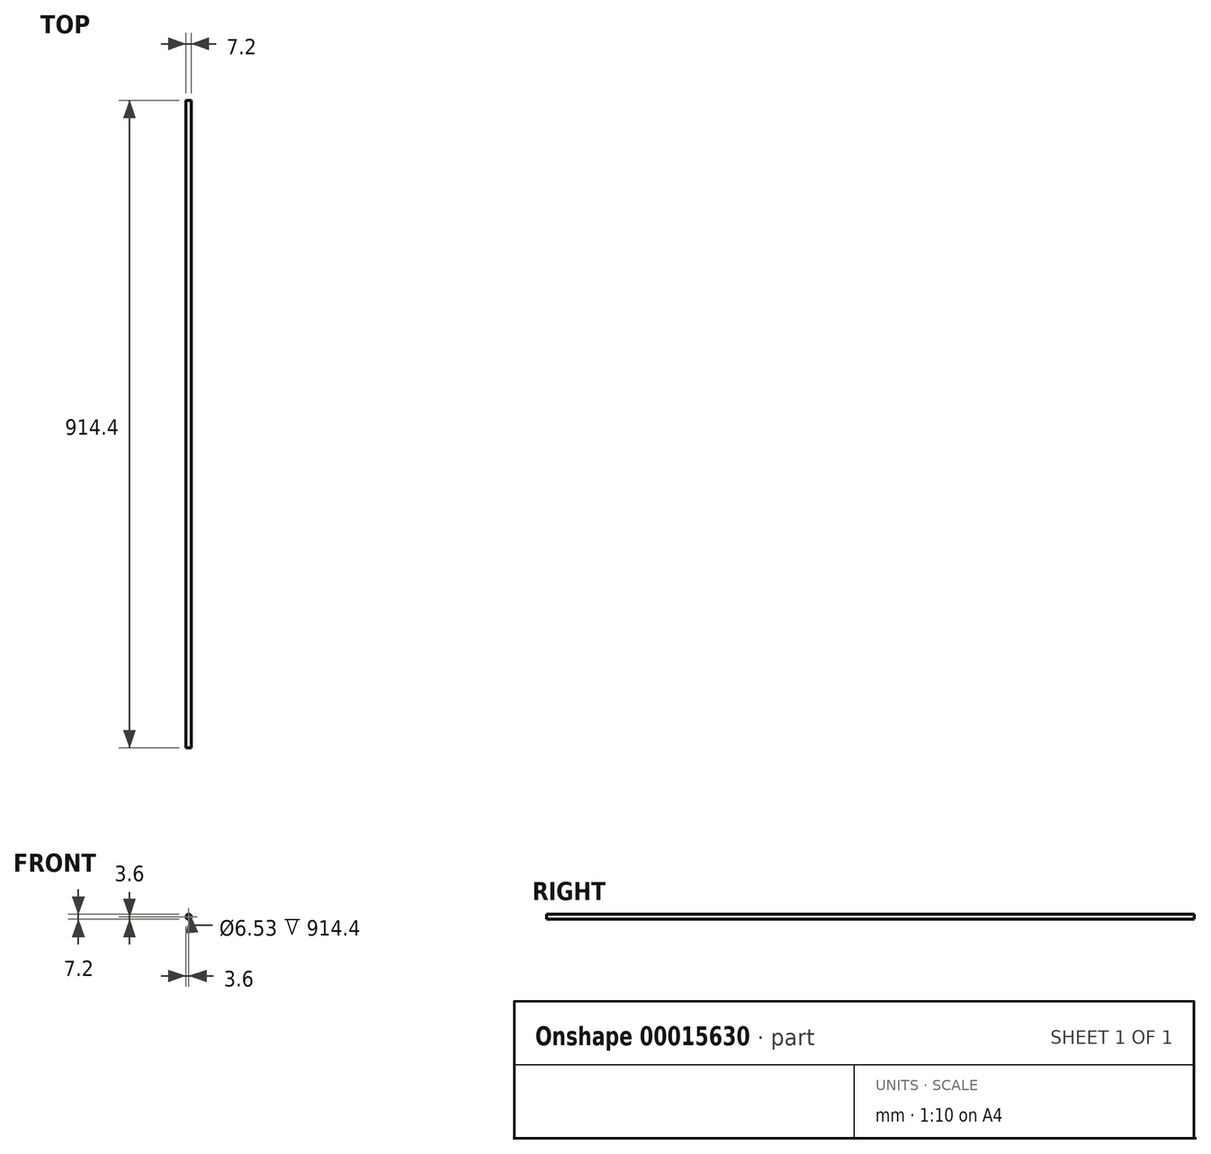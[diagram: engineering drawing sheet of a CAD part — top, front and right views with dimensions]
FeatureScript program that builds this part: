
annotation { "Feature Type Name" : "Feature", "Feature Type Description" : "" }
export const myFeature = defineFeature(function(context is Context, id is Id, definition is map)
    precondition{}
    {
        {
            var Q0;
            Q0=qCreatedBy(makeId("Front.planeOp"),FACE);
            var sketch = newSketch(context, id + "F0", { "sketchPlane" : qUnion([Q0])});
            skCircle(sketch, "E0", {"center": v(0, 0) * mm, "radius": 3.6 * mm});
            skCircle(sketch, "E1", {"center": v(0, 0) * mm, "radius": 3.27 * mm});
            skSolve(sketch);
        }
        {
            var Q0;
            Q0=makeQuery(id+"F0.imprint","IMPRINT",FACE,{"disambiguationData":[TD([[makeQuery(id+"F0.imprint","IMPRINT",EDGE,{"derivedFrom":sQuery(id+"F0.wireOp",EDGE,"E0")}),1.0]])]});
            extrude(context, id + "F1", {"entities" : qUnion([Q0]), "endBound" : BoundingType.SYMMETRIC, "depth" : 914.4 * mm});
        }
    });
